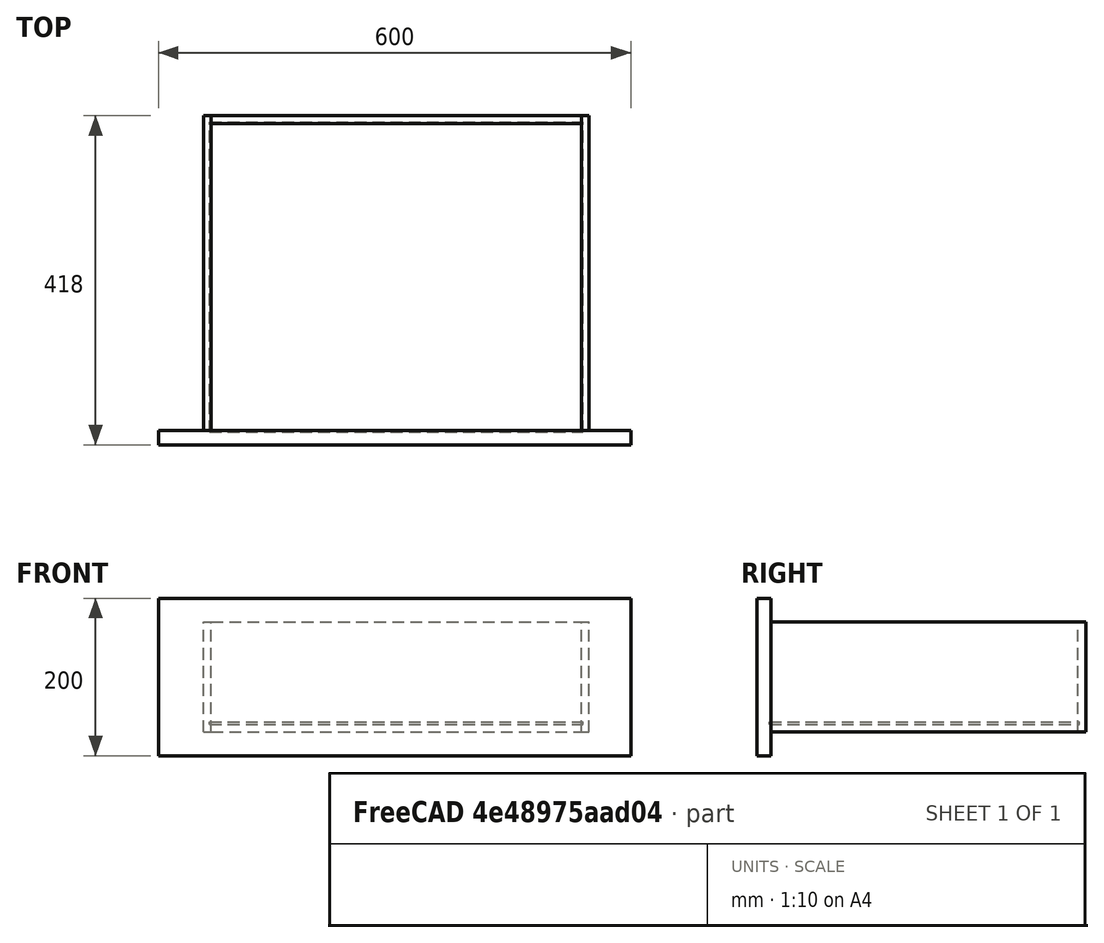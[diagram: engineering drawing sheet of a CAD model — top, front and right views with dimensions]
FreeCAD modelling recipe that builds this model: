
FCSTD DOCUMENT  (FreeCAD 0.19R24367 (Git))
Label: Demo007_drawer
License: All rights reserved
LicenseURL: http://en.wikipedia.org/wiki/All_rights_reserved
objects: Part::Box×5, Spreadsheet::Sheet×1
note: 5 computed .brp shape members not serialized (recipe doc carries the construction recipe); baked Part::Feature solids carry a one-line shape summary decoded from their .brp

FEATURE [Spreadsheet::Sheet] Spreadsheet  label="DrawerResize"
  cells = A1=Drawer width; B1(dwidth)==490mm; A2=Drawer depth; B2(ddepth)==400mm; A3=Drawer height; B3(dheight)==140mm; A4=Front width; B4(fwidth)==600mm; A5=Front height; B5(fheight)==200mm; A6=Drawer thickness; B6(dthick)==10mm; A7=Front thickness; B7(fthick)==18mm; A8=Bottom thickness; B8(bthick)==3mm; A9=Bottom offset; B9(boffset)==10mm; A10=Bottom sink; B10(bsink)==2mm
FEATURE [Part::Box] Box  label="Bottom"
  AttacherType = Attacher::AttachEngine3D
  Height = 3
  Length = 474
  Placement = pos=(0,-2,10) rot=(0,0,1;0rad)
  Width = 394
  expr: .Placement.Base.z = <<DrawerResize>>.boffset
  expr: .Placement.Base.y = -<<DrawerResize>>.bsink
  expr: Height = <<DrawerResize>>.bthick
  expr: Width = <<DrawerResize>>.ddepth - <<DrawerResize>>.dthick + 2 * <<DrawerResize>>.bsink
  expr: Length = <<DrawerResize>>.dwidth - 2 * <<DrawerResize>>.dthick + 2 * <<DrawerResize>>.bsink
FEATURE [Part::Box] Box001  label="Left"
  AttacherType = Attacher::AttachEngine3D
  Height = 140
  Length = 10
  Placement = pos=(-8,0,0) rot=(0,0,1;0rad)
  Width = 400
  expr: .Placement.Base.x = -<<DrawerResize>>.dthick + <<DrawerResize>>.bsink
  expr: Height = <<DrawerResize>>.dheight
  expr: Width = <<DrawerResize>>.ddepth
  expr: Length = <<DrawerResize>>.dthick
FEATURE [Part::Box] Box002  label="Right"
  AttacherType = Attacher::AttachEngine3D
  Height = 140
  Length = 10
  Placement = pos=(472,0,0) rot=(0,0,1;0rad)
  Width = 400
  expr: .Placement.Base.x = <<DrawerResize>>.dwidth - 2 * <<DrawerResize>>.dthick + <<DrawerResize>>.bsink
  expr: Height = <<DrawerResize>>.dheight
  expr: Width = <<DrawerResize>>.ddepth
  expr: Length = <<DrawerResize>>.dthick
FEATURE [Part::Box] Box003  label="Back"
  AttacherType = Attacher::AttachEngine3D
  Height = 140
  Length = 470
  Placement = pos=(2,390,0) rot=(0,0,1;0rad)
  Width = 10
  expr: .Placement.Base.y = <<DrawerResize>>.ddepth - <<DrawerResize>>.dthick
  expr: Height = <<DrawerResize>>.dheight
  expr: Width = <<DrawerResize>>.dthick
  expr: .Placement.Base.x = <<DrawerResize>>.bsink
  expr: Length = <<DrawerResize>>.dwidth - 2 * <<DrawerResize>>.dthick
FEATURE [Part::Box] Box004  label="Front"
  AttacherType = Attacher::AttachEngine3D
  Height = 200
  Length = 600
  Placement = pos=(-65,-18,-30) rot=(0,0,1;0rad)
  Width = 18
  expr: .Placement.Base.z = -(<<DrawerResize>>.fheight - <<DrawerResize>>.dheight) / 2
  expr: .Placement.Base.x = -(<<DrawerResize>>.fwidth - <<DrawerResize>>.dwidth) / 2 - <<DrawerResize>>.dthick
  expr: .Placement.Base.y = -<<DrawerResize>>.fthick
  expr: Height = <<DrawerResize>>.fheight
  expr: Width = <<DrawerResize>>.fthick
  expr: Length = <<DrawerResize>>.fwidth
